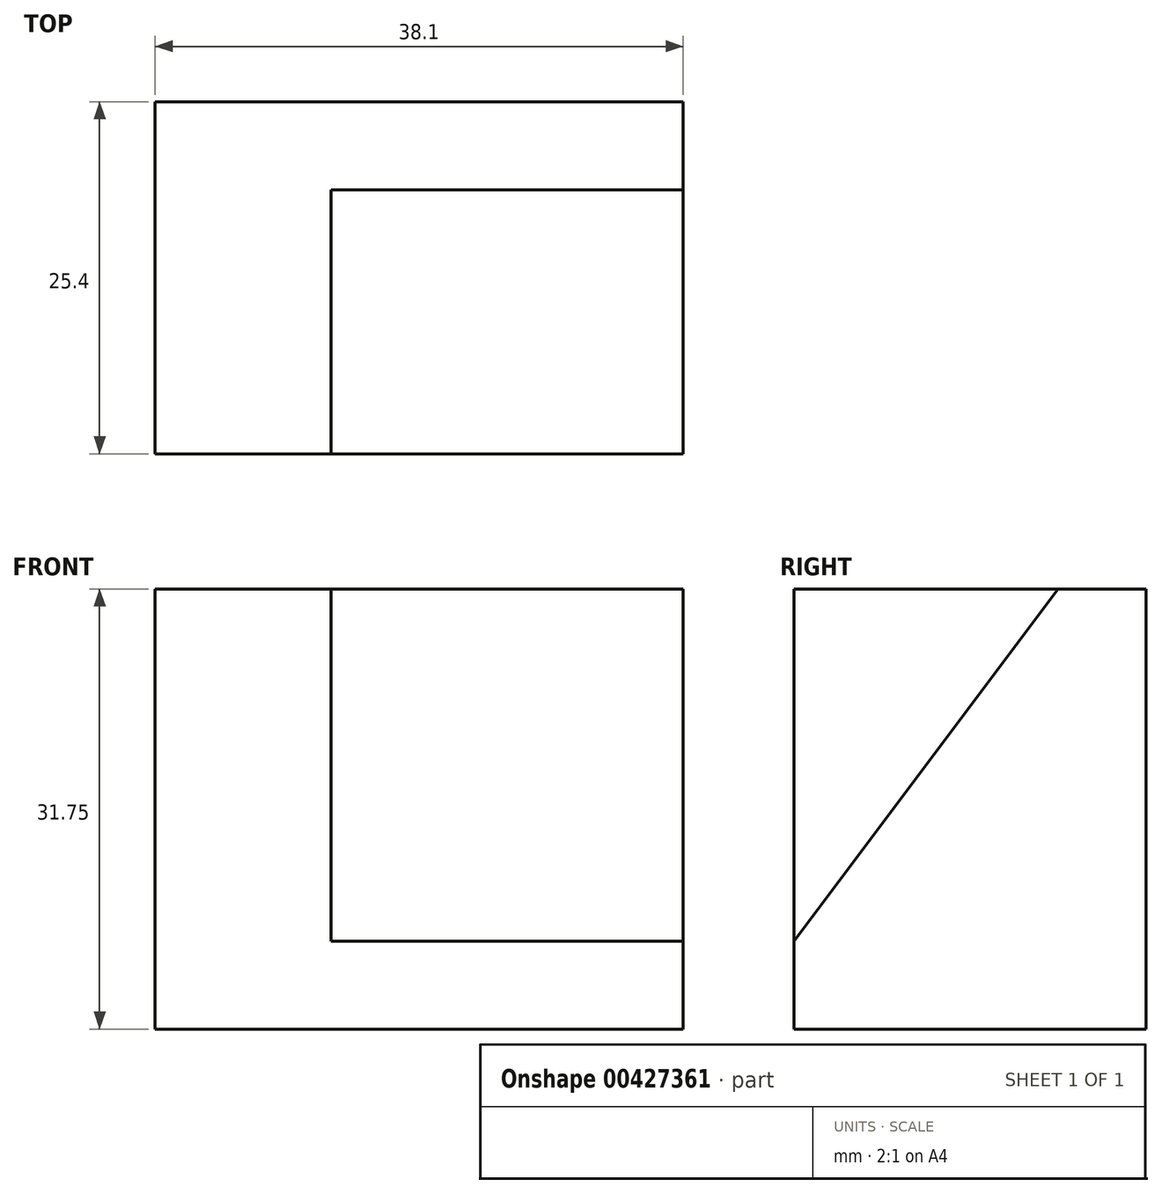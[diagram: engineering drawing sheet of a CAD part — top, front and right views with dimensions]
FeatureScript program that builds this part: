
annotation { "Feature Type Name" : "Feature", "Feature Type Description" : "" }
export const myFeature = defineFeature(function(context is Context, id is Id, definition is map)
    precondition{}
    {
        {
            var Q0;
            Q0=qCreatedBy(makeId("Right.planeOp"),FACE);
            var sketch = newSketch(context, id + "F0", { "sketchPlane" : qUnion([Q0])});
            skLineSegment(sketch, "E0", {"start": v(0, 0) * mm, "end": v(0, 31.75) * mm});
            skLineSegment(sketch, "E1", {"start": v(0, 31.75) * mm, "end": v(25.4, 31.75) * mm});
            skLineSegment(sketch, "E2", {"start": v(25.4, 31.75) * mm, "end": v(25.4, 0) * mm});
            skLineSegment(sketch, "E3", {"start": v(0, 0) * mm, "end": v(25.4, 0) * mm});
            skLineSegment(sketch, "E4", {"start": v(0, 0) * mm, "end": v(0, 6.35) * mm});
            skLineSegment(sketch, "E5", {"start": v(25.4, 31.75) * mm, "end": v(19.05, 31.75) * mm});
            skLineSegment(sketch, "E6", {"start": v(19.05, 31.75) * mm, "end": v(0, 6.35) * mm});
            skSolve(sketch);
        }
        {
            var Q0;
            Q0=makeQuery(id+"F0.imprint","IMPRINT",FACE,{"disambiguationData":[TD([[makeQuery(id+"F0.imprint","IMPRINT",EDGE,{"derivedFrom":sQuery(id+"F0.wireOp",EDGE,"E2")}),-1.0]])]});
            extrude(context, id + "F1", {"entities" : qUnion([Q0]), "depth" : 25.4 * mm});
        }
        {
            var Q0;
            Q0=qCreatedBy(makeId("Right.planeOp"),FACE);
            var sketch = newSketch(context, id + "F2", { "sketchPlane" : qUnion([Q0])});
            skLineSegment(sketch, "E7", {"start": v(25.4, 0) * mm, "end": v(25.4, 31.75) * mm});
            skLineSegment(sketch, "E8", {"start": v(25.4, 31.75) * mm, "end": v(0, 31.75) * mm});
            skLineSegment(sketch, "E9", {"start": v(0, 31.75) * mm, "end": v(0, 0) * mm});
            skLineSegment(sketch, "E10", {"start": v(25.4, 0) * mm, "end": v(0, 0) * mm});
            skSolve(sketch);
        }
        {
            var Q0;
            Q0=makeQuery(id+"F2.imprint","IMPRINT",FACE,{"disambiguationData":[TD([[makeQuery(id+"F2.imprint","IMPRINT",EDGE,{"derivedFrom":sQuery(id+"F2.wireOp",EDGE,"E7")}),1.0]])]});
            extrude(context, id + "F3", {"entities" : qUnion([Q0]), "operationType" : NewBodyOperationType.ADD, "oppositeDirection" : true, "depth" : 12.7 * mm});
        }
    });
